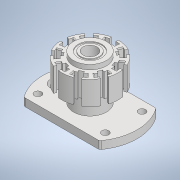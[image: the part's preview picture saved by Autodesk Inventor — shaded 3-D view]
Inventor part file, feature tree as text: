
AUTODESK INVENTOR PART (.ipt)
format: ipt  version: 2020 (Build 240168000, 168)  size: 542,208 bytes
history: native  units: mm
features: extrude x11, sketch x11, projected_geometry x9, thicken_offset x4, pattern_circular x2, fillet x2
ambient origin geometry x8: Origin, YZ Plane, XZ Plane, XY Plane, X Axis, Y Axis, Z Axis, Center Point
bodies: Solid1 (feature_tree)
feature tree (39):
  extrude  "Extrusion1"  Depth=12.0mm
  extrude  "Extrusion2"  Depth=1.65mm TaperAngle=0.0deg
  extrude  "Extrusion3"  Depth=1.0mm TaperAngle=0.0deg
  extrude  "Extrusion4"  Depth=2.2mm TaperAngle=0.0deg
  extrude  "Extrusion5"  Depth=12.0mm
  extrude  "Extrusion6"  Depth=4.712389mm
  extrude  "Extrusion7"  Depth=8.0mm
  pattern_circular  "Circular Pattern1"  [2 undecoded]
  extrude  "Extrusion8"  Depth=0.2mm TaperAngle=360.0deg
  extrude  "Extrusion9"  Depth=0.2mm
  fillet  "Fillet1"  Radius=5.0mm
  pattern_circular  "Circular Pattern2"  [2 undecoded]
  extrude  "Extrusion10"  Depth=0.2mm
  extrude  "Extrusion11"  Depth=0.2mm TaperAngle=0.0deg
  fillet  "Fillet2"  Radius=0.2mm
  thicken_offset  "Thicken1"
  thicken_offset  "Thicken2"
  thicken_offset  "Thicken3"
  thicken_offset  "Thicken4"
  sketch  "Sketch1"  dims[d0=20.0mm d1=12.0mm]
  sketch  "Sketch2"  dims[d2=20.0mm d3=1.65mm d4=0.0mm]
  sketch  "Sketch3"  dims[d5=7.0mm d6=1.0mm d7=0.0mm]
  sketch  "Sketch4"  dims[d8=2.0mm d9=2.2mm d10=0.0mm]
  sketch  "Sketch5"  dims[d11=3.5mm d12=0.0mm d13=12.0mm]
  projected_geometry  "Projected Loop1"
  sketch  "Sketch6"  dims[d14=11.0mm d15=4.712389mm]
  projected_geometry  "Projected Loop2"
  projected_geometry  "Projected Loop3"
  sketch  "Sketch7"  dims[d16=4.0mm d17=0.0mm d18=8.0mm]
  projected_geometry  "Projected Loop4"
  projected_geometry  "Projected Loop5"
  sketch  "Sketch8"  dims[d19=9.0mm]
  projected_geometry  "Projected Loop6"
  sketch  "Sketch9"  dims[d20=4.0mm d21=0.0mm]
  projected_geometry  "Projected Loop7"
  sketch  "Sketch10"  dims[d22=1.22173mm]
  projected_geometry  "Projected Loop8"
  sketch  "Sketch11"  dims[d23=1.22173mm d24=4.0mm d25=0.0mm d26=90.0mm d27=360.0deg d29=3.0mm d30=5.0mm d31=0.0mm d32=4.0mm d33=5.0mm d34=0.2mm d35=0.0mm d36=0.2mm d37=90.0mm d38=360.0deg d40=7.8mm d41=14.3mm d42=1.5mm d43=1.5mm d44=1.5mm d45=1.5mm d46=2.0mm d47=0.0mm d48=7.0mm d49=3.0mm d50=2.0mm d51=0.0mm d52=0.5mm d53=1.0mm d54=1.0mm d55=1.0mm d56=1.0mm d57=1.0mm d58=1.0mm d59=1.0mm d60=1.0mm]
  projected_geometry  "Projected Loop9"
note: 4 required parameter values undecoded (feature->parameter linkage not recoverable at this tier; creation-order binding heuristic only, values carry confidence <= 0.55)
